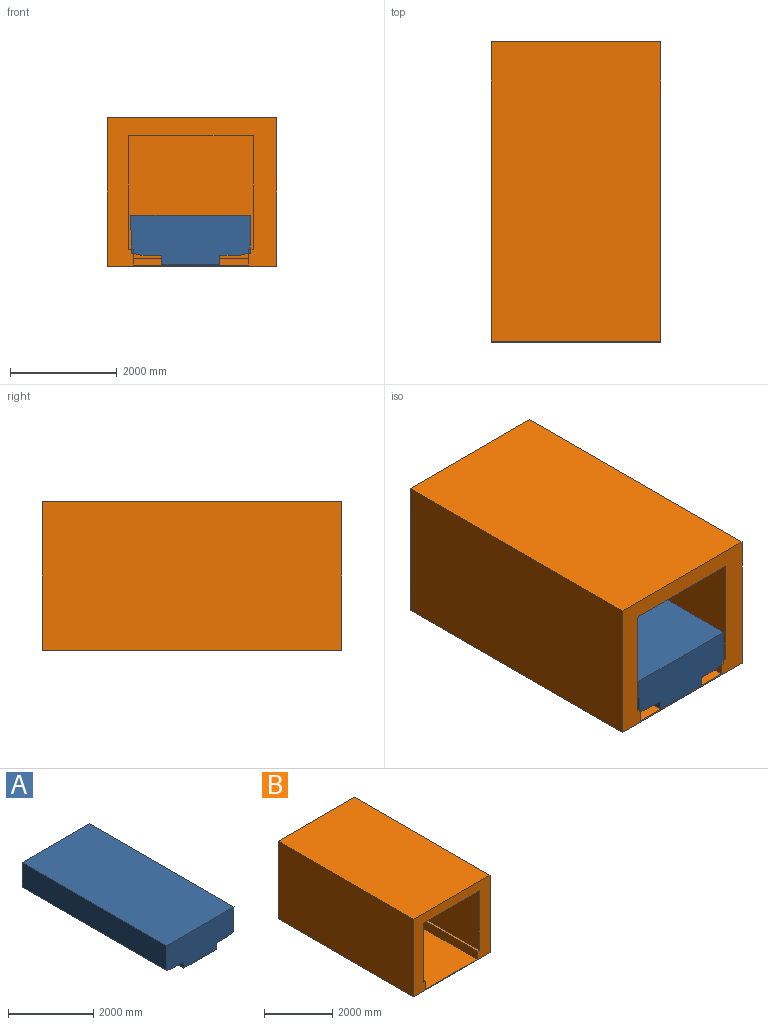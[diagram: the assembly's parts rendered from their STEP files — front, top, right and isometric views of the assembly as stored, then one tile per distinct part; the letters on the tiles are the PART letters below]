
ASSEMBLY  parts=2 mates=1
PART A: 12 faces, bbox 2250x4800x930 mm
  f0: plane 4800x1082.11mm, normal (0,0,-1), area 5194134mm2, adj f1,f2,f6,f11
  f1: plane 2250x930mm, normal (0,1,0), area 1866380mm2, adj f0,f3,f4,f5,f6,f7,f8,f9
  f2: plane 2250x930mm, normal (0,-1,0), area 1866380mm2, adj f0,f3,f4,f5,f6,f7,f8,f9
  f3: plane 4800x2250mm, normal (0,0,1), area 10800000mm2, adj f1,f2,f5,f8
  f4: plane 4800x200mm, normal (-0.2,0,-0.98), area 979011.7mm2, adj f1,f2,f5,f7
  f5: plane 4800x710mm, normal (-1,0,-0.01), area 3408338mm2, adj f1,f2,f3,f4
  f6: plane 4800x180mm, normal (-1,0,0), area 864000mm2, adj f0,f1,f2,f7
  f7: plane 4800x373.94mm, normal (0,0,-1), area 1794933mm2, adj f1,f2,f4,f6
  f8: plane 4800x710mm, normal (1,0,-0.01), area 3408338mm2, adj f1,f2,f3,f9
  f9: plane 4800x200mm, normal (0.2,0,-0.98), area 979011.7mm2, adj f1,f2,f8,f10
  f10: plane 4800x373.94mm, normal (0,0,-1), area 1794933mm2, adj f1,f2,f9,f11
  f11: plane 4800x180mm, normal (1,0,0), area 864000mm2, adj f0,f1,f2,f10
PART B: 17 faces, bbox 3179.1x5626.1x2789.4 mm
  f0: plane 2336.8x2298.7mm, normal (0,-1,0), area 5342247.4mm2, adj f1,f4,f8,f9,f13,f14,f15,f16
  f1: plane 2159x177.8mm, normal (0,0,1), area 383870.2mm2, adj f0,f2,f13,f15
  f2: plane 2159x127mm, normal (0,-1,0), area 274193mm2, adj f1,f3,f13,f15
  f3: plane 5143.5x2159mm, normal (0,0,1), area 11104816.5mm2, adj f2,f11,f13,f15
  f4: plane 5321.3x2133.6mm, normal (-1,0,0), area 11353525.7mm2, adj f0,f9,f11,f16
  f5: plane 5626.1x3179.12mm, normal (0,0,1), area 17886061.5mm2, adj f6,f10,f11,f12
  f6: plane 5626.1x2789.39mm, normal (-1,0,0), area 15693401.7mm2, adj f5,f7,f11,f12
  f7: plane 5626.1x3179.12mm, normal (0,0,-1), area 17886061.5mm2, adj f6,f10,f11,f12
  f8: plane 5321.3x2133.6mm, normal (1,0,0), area 11353525.7mm2, adj f0,f9,f11,f14
  f9: plane 5321.3x2336.8mm, normal (0,0,-1), area 12434813.8mm2, adj f0,f4,f8,f11
  f10: plane 5626.1x2789.39mm, normal (1,0,0), area 15693401.7mm2, adj f5,f7,f11,f12
  f11: plane 3179.12x2789.39mm, normal (0,-1,0), area 3251380.6mm2, adj f3,f4,f5,f6,f7,f8,f9,f10
  f12: plane 3179.12x2789.39mm, normal (0,1,0), area 8867820.9mm2, adj f5,f6,f7,f10
  f13: plane 5321.3x292.1mm, normal (1,0,0), area 1531771.1mm2, adj f0,f1,f2,f3,f11,f14
  f14: plane 5321.3x88.9mm, normal (0,0,1), area 473063.6mm2, adj f0,f8,f11,f13
  f15: plane 5321.3x292.1mm, normal (-1,0,0), area 1531771.1mm2, adj f0,f1,f2,f3,f11,f16
  f16: plane 5321.3x88.9mm, normal (0,0,1), area 473063.6mm2, adj f0,f4,f11,f15
PLACE A t=(-3347.05,-4492.36,-1822.46)mm
PLACE B t=(-2261.73,828.94,-1152.29)mm fixed
MATE planar A.f2 <-> B.f11  axis (0,-1,0) through (-2222.05,-4492.36,-1313.91)mm
